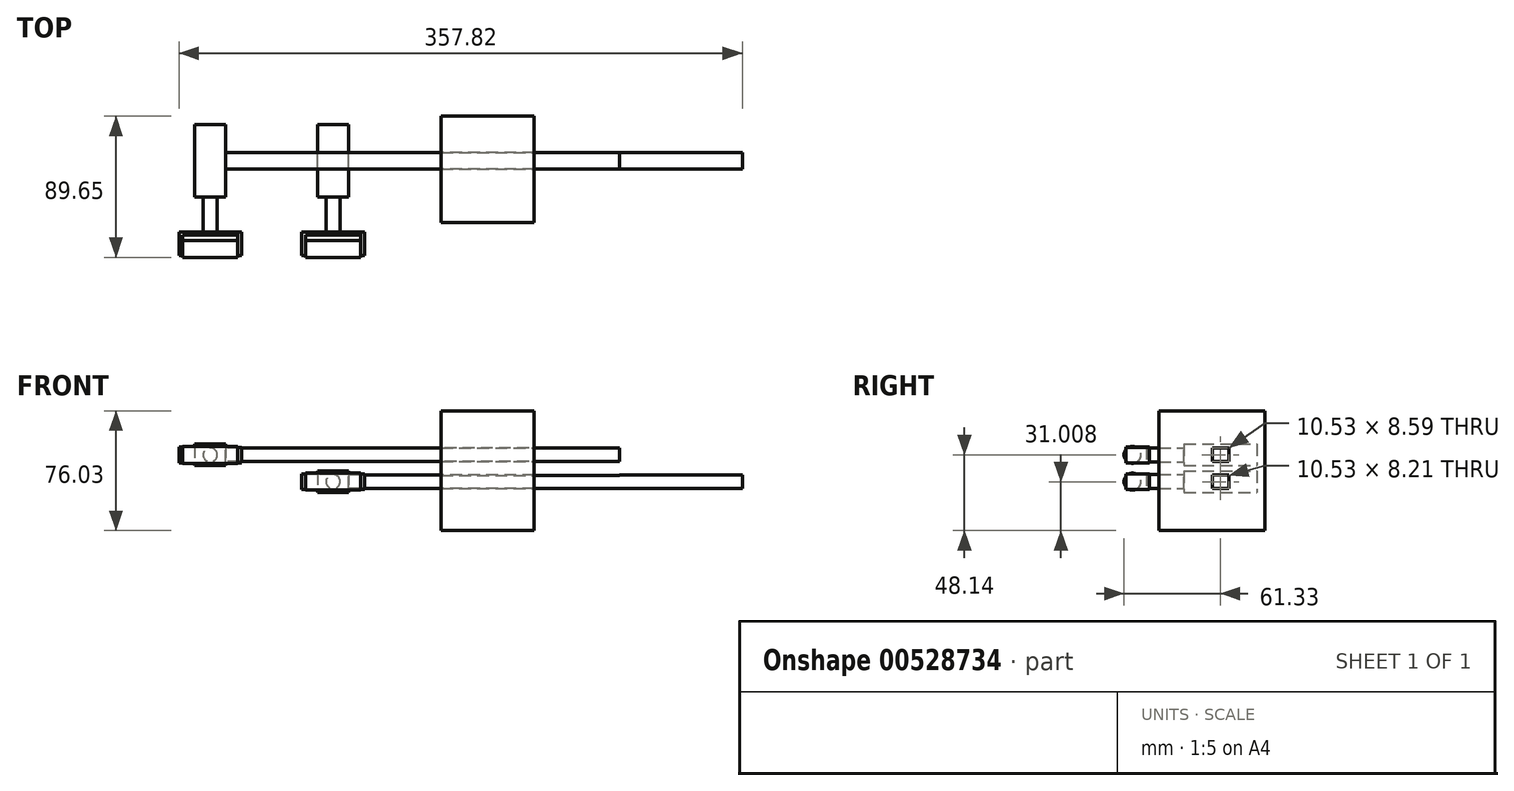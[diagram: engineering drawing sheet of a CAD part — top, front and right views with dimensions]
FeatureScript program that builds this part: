
annotation { "Feature Type Name" : "Feature", "Feature Type Description" : "" }
export const myFeature = defineFeature(function(context is Context, id is Id, definition is map)
    precondition{}
    {
        {
            var Q0;
            Q0=qCreatedBy(makeId("Right.planeOp"),FACE);
            var sketch = newSketch(context, id + "F0", { "sketchPlane" : qUnion([Q0])});
            skLineSegment(sketch, "E0.bottom", {"start": v(-5.26, -4.3) * mm, "end": v(5.26, -4.3) * mm});
            skLineSegment(sketch, "E0.top", {"start": v(-5.26, 4.3) * mm, "end": v(5.26, 4.3) * mm});
            skLineSegment(sketch, "E0.left", {"start": v(-5.26, -4.3) * mm, "end": v(-5.26, 4.3) * mm});
            skLineSegment(sketch, "E0.right", {"start": v(5.26, -4.3) * mm, "end": v(5.26, 4.3) * mm});
            skPoint(sketch, "E0.middle", {"position": v(0, 0) * mm});
            skSolve(sketch);
        }
        {
            var Q0;
            Q0 = qSketchRegion(id + "F0", true);
            extrude(context, id + "F1", {"entities" : qUnion([Q0]), "depth" : 250 * mm, "offsetDistance" : 25 * mm});
        }
        {
            var Q0;
            Q0=makeQuery(id+"F1.opExtrude","CAP_FACE",FACE,{"disambiguationData":[OSD([sQuery(id+"F0.wireOp",EDGE,"E0.bottom"),sQuery(id+"F0.wireOp",EDGE,"E0.top"),sQuery(id+"F0.wireOp",EDGE,"E0.left"),sQuery(id+"F0.wireOp",EDGE,"E0.right")])],"isStart":true});
            var sketch = newSketch(context, id + "F2", { "sketchPlane" : qUnion([Q0])});
            skLineSegment(sketch, "E1.bottom", {"start": v(23.08, 6.8) * mm, "end": v(-23.08, 6.8) * mm});
            skLineSegment(sketch, "E1.top", {"start": v(23.08, -6.8) * mm, "end": v(-23.08, -6.8) * mm});
            skLineSegment(sketch, "E1.left", {"start": v(23.08, 6.8) * mm, "end": v(23.08, -6.8) * mm});
            skLineSegment(sketch, "E1.right", {"start": v(-23.08, 6.8) * mm, "end": v(-23.08, -6.8) * mm});
            skPoint(sketch, "E1.middle", {"position": v(0, 0) * mm});
            skSolve(sketch);
        }
        {
            var Q0;
            Q0 = qSketchRegion(id + "F2", true);
            extrude(context, id + "F3", {"entities" : qUnion([Q0]), "operationType" : NewBodyOperationType.ADD, "depth" : 19.8 * mm, "offsetDistance" : 25 * mm});
        }
        {
            var Q0;
            Q0=makeQuery(id+"F3.opExtrude","SWEPT_FACE",FACE,{"disambiguationData":[OSD([sQuery(id+"F2.wireOp",EDGE,"E1.left")])]});
            var sketch = newSketch(context, id + "F4", { "sketchPlane" : qUnion([Q0])});
            skLineSegment(sketch, "E2", {"start": v(0, 0) * mm, "end": v(-19.8, 0) * mm, "construction": true});
            skCircle(sketch, "E3", {"center": v(-9.9, 0) * mm, "radius": 4.48 * mm});
            skSolve(sketch);
        }
        {
            var Q0;
            Q0 = qSketchRegion(id + "F4", true);
            extrude(context, id + "F5", {"entities" : qUnion([Q0]), "operationType" : NewBodyOperationType.ADD, "depth" : 22 * mm, "offsetDistance" : 25 * mm});
        }
        {
            var Q0;
            Q0=makeQuery(id+"F5.opExtrude","CAP_FACE",FACE,{"disambiguationData":[OSD([sQuery(id+"F4.wireOp",EDGE,"E3")])],"isStart":false});
            var sketch = newSketch(context, id + "F6", { "sketchPlane" : qUnion([Q0])});
            skLineSegment(sketch, "E4.bottom", {"start": v(-27.32, 5) * mm, "end": v(7.52, 5) * mm});
            skLineSegment(sketch, "E4.top", {"start": v(-27.32, -5) * mm, "end": v(7.52, -5) * mm});
            skLineSegment(sketch, "E4.left", {"start": v(-27.32, 5) * mm, "end": v(-27.32, -5) * mm});
            skLineSegment(sketch, "E4.right", {"start": v(7.52, 5) * mm, "end": v(7.52, -5) * mm});
            skPoint(sketch, "E4.middle", {"position": v(-9.9, 0) * mm});
            skSolve(sketch);
        }
        {
            var Q0;
            Q0 = qSketchRegion(id + "F6", true);
            extrude(context, id + "F7", {"entities" : qUnion([Q0]), "operationType" : NewBodyOperationType.ADD, "depth" : 2.1 * mm, "offsetDistance" : 25 * mm});
        }
        {
            var Q0;
            Q0=makeQuery(id+"F7.opExtrude","SWEPT_FACE",FACE,{"disambiguationData":[OSD([sQuery(id+"F6.wireOp",EDGE,"E4.right")])]});
            var sketch = newSketch(context, id + "F8", { "sketchPlane" : qUnion([Q0])});
            skLineSegment(sketch, "E5.bottom", {"start": v(-45.08, -5) * mm, "end": v(-60.08, -5) * mm});
            skLineSegment(sketch, "E5.top", {"start": v(-45.08, 4.7) * mm, "end": v(-60.08, 4.7) * mm});
            skLineSegment(sketch, "E5.left", {"start": v(-45.08, -5) * mm, "end": v(-45.08, 4.7) * mm});
            skLineSegment(sketch, "E5.right", {"start": v(-60.08, -5) * mm, "end": v(-60.08, 4.7) * mm});
            skSolve(sketch);
        }
        {
            var Q0;
            Q0 = qSketchRegion(id + "F8", true);
            extrude(context, id + "F9", {"entities" : qUnion([Q0]), "operationType" : NewBodyOperationType.ADD, "depth" : 2.5 * mm, "offsetDistance" : 25 * mm});
        }
        {
            var Q0;
            Q0=makeQuery(id+"F7.opExtrude","SWEPT_FACE",FACE,{"disambiguationData":[OSD([sQuery(id+"F6.wireOp",EDGE,"E4.left")])]});
            var sketch = newSketch(context, id + "F10", { "sketchPlane" : qUnion([Q0])});
            skLineSegment(sketch, "E6.bottom", {"start": v(45.08, -5) * mm, "end": v(60.08, -5) * mm});
            skLineSegment(sketch, "E6.top", {"start": v(45.08, 5) * mm, "end": v(60.08, 5) * mm});
            skLineSegment(sketch, "E6.left", {"start": v(45.08, -5) * mm, "end": v(45.08, 5) * mm});
            skLineSegment(sketch, "E6.right", {"start": v(60.08, -5) * mm, "end": v(60.08, 5) * mm});
            skSolve(sketch);
        }
        {
            var Q0;
            Q0 = qSketchRegion(id + "F10", true);
            extrude(context, id + "F11", {"entities" : qUnion([Q0]), "operationType" : NewBodyOperationType.ADD, "depth" : 2.5 * mm, "offsetDistance" : 25 * mm});
        }
        {
            var Q0;
            Q0=makeQuery(id+"F9.opExtrude","CAP_FACE",FACE,{"disambiguationData":[OSD([sQuery(id+"F8.wireOp",EDGE,"E5.bottom"),sQuery(id+"F8.wireOp",EDGE,"E5.top"),sQuery(id+"F8.wireOp",EDGE,"E5.left"),sQuery(id+"F8.wireOp",EDGE,"E5.right")])],"isStart":true});
            var sketch = newSketch(context, id + "F12", { "sketchPlane" : qUnion([Q0])});
            skCircle(sketch, "E7", {"center": v(55.93, 0) * mm, "radius": 5.4 * mm});
            skSolve(sketch);
        }
        {
            var Q0;
            Q0 = qSketchRegion(id + "F12", true);
            extrude(context, id + "F13", {"entities" : qUnion([Q0]), "operationType" : NewBodyOperationType.ADD, "depth" : 34.9 * mm, "offsetDistance" : 25 * mm});
        }
        {
            var Q0;
            {var subQ0=sQuery(id+"F0.wireOp",EDGE,"E0.right");var subQ1=sQuery(id+"F0.wireOp",EDGE,"E0.left");var subQ2=sQuery(id+"F0.wireOp",EDGE,"E0.top");var subQ3=sQuery(id+"F0.wireOp",EDGE,"E0.bottom");Q0=makeQuery(id+"FnNemLCz8G5RFul_1.boolean.opBoolean","MERGE",FACE,{"derivedFrom":[makeQuery(id+"F1.opExtrude","CAP_FACE",FACE,{"disambiguationData":[OSD([subQ3,subQ2,subQ1,subQ0])],"isStart":false}),makeQuery(id+"FnNemLCz8G5RFul_1.opExtrude","CAP_FACE",FACE,{"disambiguationData":[OSD([subQ3,subQ2,subQ1,subQ0,sQuery(id+"FaEyFqlGZM1JVYV_1.wireOp",EDGE,"f9RV9EYd-t6Su-KvJ8-cTsO-nnxuvdrn0u89.bottom"),sQuery(id+"FaEyFqlGZM1JVYV_1.wireOp",EDGE,"f9RV9EYd-t6Su-KvJ8-cTsO-nnxuvdrn0u89.top"),sQuery(id+"FaEyFqlGZM1JVYV_1.wireOp",EDGE,"f9RV9EYd-t6Su-KvJ8-cTsO-nnxuvdrn0u89.left"),sQuery(id+"FaEyFqlGZM1JVYV_1.wireOp",EDGE,"f9RV9EYd-t6Su-KvJ8-cTsO-nnxuvdrn0u89.right")])],"isStart":true})]});}
            var sketch = newSketch(context, id + "F14", { "sketchPlane" : qUnion([Q0])});
            skLineSegment(sketch, "E8.bottom", {"start": v(-21.63, -27.03) * mm, "end": v(21.63, -27.03) * mm});
            skLineSegment(sketch, "E8.top", {"start": v(-21.63, 27.03) * mm, "end": v(21.63, 27.03) * mm});
            skLineSegment(sketch, "E8.left", {"start": v(-21.63, -27.03) * mm, "end": v(-21.63, 27.03) * mm});
            skLineSegment(sketch, "E8.right", {"start": v(21.63, -27.03) * mm, "end": v(21.63, 27.03) * mm});
            skPoint(sketch, "E8.middle", {"position": v(0, 0) * mm});
            skLineSegment(sketch, "E9.bottom", {"start": v(-5.26, -4.3) * mm, "end": v(5.26, -4.3) * mm});
            skLineSegment(sketch, "E9.top", {"start": v(-5.26, 4.3) * mm, "end": v(5.26, 4.3) * mm});
            skLineSegment(sketch, "E9.left", {"start": v(-5.26, -4.3) * mm, "end": v(-5.26, 4.3) * mm});
            skLineSegment(sketch, "E9.right", {"start": v(5.26, -4.3) * mm, "end": v(5.26, 4.3) * mm});
            skSolve(sketch);
        }
        {
            var Q0;
            Q0 = qSketchRegion(id + "F14", true);
            extrude(context, id + "F15", {"entities" : qUnion([Q0]), "operationType" : NewBodyOperationType.REMOVE, "oppositeDirection" : true, "depth" : 135 * mm, "offsetDistance" : 25 * mm});
        }
        {
            var Q0;
            Q0=makeQuery(id+"F1.opExtrude","SWEPT_BODY",BODY,{"disambiguationData":[OSD([sQuery(id+"F0.wireOp",EDGE,"E0.bottom"),sQuery(id+"F0.wireOp",EDGE,"E0.top"),sQuery(id+"F0.wireOp",EDGE,"E0.left"),sQuery(id+"F0.wireOp",EDGE,"E0.right")])]});
            transform(context, id + "F16", {"entities" : qUnion([Q0]), "transformType" : TransformType.TRANSLATION_3D, "dx" : -103 * mm, "dy" : 0 * mm, "dz" : 113 * mm, "makeCopy" : true});
        }
        {
            var Q0;
            Q0=makeQuery(id+"F16.opPattern","COPY",BODY,{"derivedFrom":makeQuery(id+"F1.opExtrude","SWEPT_BODY",BODY,{"disambiguationData":[OSD([sQuery(id+"F0.wireOp",EDGE,"E0.bottom"),sQuery(id+"F0.wireOp",EDGE,"E0.top"),sQuery(id+"F0.wireOp",EDGE,"E0.left"),sQuery(id+"F0.wireOp",EDGE,"E0.right")])]}),"instanceName":"1"});
            deleteBodies(context, id + "F17", {"entities" : qUnion([Q0])});
        }
        {
            var Q0;
            Q0=makeQuery(id+"F1.opExtrude","SWEPT_BODY",BODY,{"disambiguationData":[OSD([sQuery(id+"F0.wireOp",EDGE,"E0.bottom"),sQuery(id+"F0.wireOp",EDGE,"E0.top"),sQuery(id+"F0.wireOp",EDGE,"E0.left"),sQuery(id+"F0.wireOp",EDGE,"E0.right")])]});
            transform(context, id + "F18", {"entities" : qUnion([Q0]), "transformType" : TransformType.TRANSLATION_3D, "dx" : -78 * mm, "dy" : 0 * mm, "dz" : 17 * mm, "makeCopy" : true});
        }
        {
            var Q0;
            Q0=makeQuery(id+"F18.opPattern","COPY",FACE,{"derivedFrom":makeQuery(id+"F1.opExtrude","CAP_FACE",FACE,{"disambiguationData":[OSD([sQuery(id+"F0.wireOp",EDGE,"E0.bottom"),sQuery(id+"F0.wireOp",EDGE,"E0.top"),sQuery(id+"F0.wireOp",EDGE,"E0.left"),sQuery(id+"F0.wireOp",EDGE,"E0.right")])],"isStart":false}),"instanceName":"1"});
            var sketch = newSketch(context, id + "F19", { "sketchPlane" : qUnion([Q0])});
            skLineSegment(sketch, "E10.bottom", {"start": v(28.32, 44.9) * mm, "end": v(-39.08, 44.9) * mm});
            skLineSegment(sketch, "E10.top", {"start": v(28.32, -31.14) * mm, "end": v(-39.08, -31.14) * mm});
            skLineSegment(sketch, "E10.left", {"start": v(28.32, 44.9) * mm, "end": v(28.32, -31.14) * mm});
            skLineSegment(sketch, "E10.right", {"start": v(-39.08, 44.9) * mm, "end": v(-39.08, -31.14) * mm});
            skLineSegment(sketch, "E11.bottom", {"start": v(5.26, 21.3) * mm, "end": v(-5.26, 21.3) * mm});
            skLineSegment(sketch, "E11.top", {"start": v(5.26, 12.7) * mm, "end": v(-5.26, 12.7) * mm});
            skLineSegment(sketch, "E11.left", {"start": v(5.26, 21.3) * mm, "end": v(5.26, 12.7) * mm});
            skLineSegment(sketch, "E11.right", {"start": v(-5.26, 21.3) * mm, "end": v(-5.26, 12.7) * mm});
            skLineSegment(sketch, "E12.bottom", {"start": v(5.26, 3.97) * mm, "end": v(-5.26, 3.97) * mm});
            skLineSegment(sketch, "E12.top", {"start": v(5.26, -4.24) * mm, "end": v(-5.26, -4.24) * mm});
            skLineSegment(sketch, "E12.left", {"start": v(5.26, 3.97) * mm, "end": v(5.26, -4.24) * mm});
            skLineSegment(sketch, "E12.right", {"start": v(-5.26, 3.97) * mm, "end": v(-5.26, -4.24) * mm});
            skSolve(sketch);
        }
        {
            var Q0;
            Q0 = qSketchRegion(id + "F19", true);
            extrude(context, id + "F20", {"entities" : qUnion([Q0]), "oppositeDirection" : true, "depth" : 113.3 * mm, "offsetDistance" : 25 * mm});
        }
        {
            var Q0;
            Q0=makeQuery(id+"F20.opExtrude","CAP_FACE",FACE,{"disambiguationData":[OSD([sQuery(id+"F19.wireOp",EDGE,"E10.bottom"),sQuery(id+"F19.wireOp",EDGE,"E10.top"),sQuery(id+"F19.wireOp",EDGE,"E10.left"),sQuery(id+"F19.wireOp",EDGE,"E10.right"),sQuery(id+"F19.wireOp",EDGE,"E11.bottom"),sQuery(id+"F19.wireOp",EDGE,"E11.top"),sQuery(id+"F19.wireOp",EDGE,"E11.left"),sQuery(id+"F19.wireOp",EDGE,"E11.right"),sQuery(id+"F19.wireOp",EDGE,"E12.bottom"),sQuery(id+"F19.wireOp",EDGE,"E12.top"),sQuery(id+"F19.wireOp",EDGE,"E12.left"),sQuery(id+"F19.wireOp",EDGE,"E12.right")])],"isStart":true});
            extrude(context, id + "F21", {"entities" : qUnion([Q0]), "operationType" : NewBodyOperationType.REMOVE, "oppositeDirection" : true, "depth" : 54.1 * mm, "offsetDistance" : 25 * mm});
        }
    });
